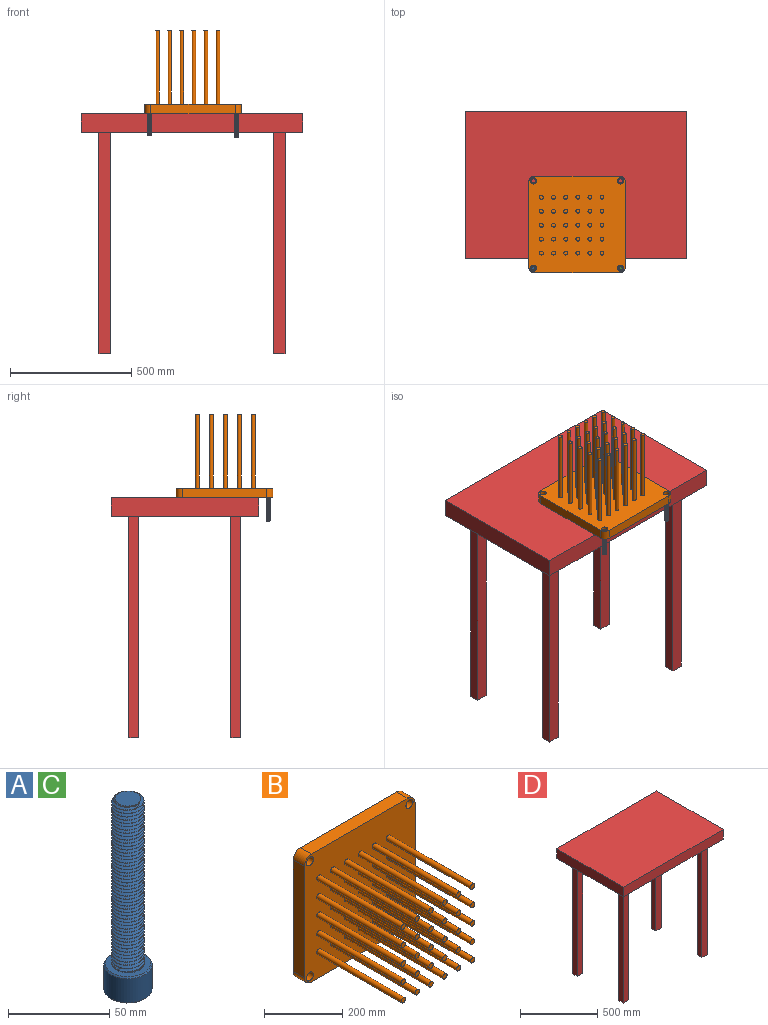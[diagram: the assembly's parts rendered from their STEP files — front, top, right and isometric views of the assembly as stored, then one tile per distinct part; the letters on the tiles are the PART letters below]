
ASSEMBLY  parts=4 mates=3
PART A: 74 faces, bbox 27.1x27.1x119.6 mm
  f0: cone r=8mm half-angle=67.5deg, axis (0,0,-1), area 33.3mm2, adj f6,f56,f57,f58
  f1: cone r=12mm half-angle=45deg, axis (0,0,-1), area 74.5mm2, adj f4,f61
  f2: cone r=11.28mm half-angle=45deg, axis (0,0,1), area 74.5mm2, adj f4,f60
  f3: cone r=8.08mm half-angle=45deg, axis (0,0,-1), area 6.2mm2, adj f60,f72
  f4: cylinder r=12mm len=24mm, axis (0,0,1), area 1097.8mm2, adj f1,f2
  f5: cone r=6.45mm half-angle=55deg, axis (0,0,-1), area 48.6mm2, adj f6,f7,f57,f58,f59
  f6: cylinder r=6.7mm len=98.78mm, axis (0,0,-1), area 519.9mm2, adj f0,f5,f57,f58
  f7: cylinder r=8mm len=16mm, axis (0,0,1), area 9.7mm2, adj f5,f8,f57,f58
  f8: cylinder r=8mm len=16mm, axis (0,0,1), area 12.6mm2, adj f7,f9,f57,f58
  f9: cylinder r=8mm len=16mm, axis (0,0,1), area 12.6mm2, adj f8,f10,f57,f58
  f10: cylinder r=8mm len=16mm, axis (0,0,1), area 12.6mm2, adj f9,f11,f57,f58
  f11: cylinder r=8mm len=16mm, axis (0,0,1), area 12.6mm2, adj f10,f12,f57,f58
  f12: cylinder r=8mm len=16mm, axis (0,0,1), area 12.6mm2, adj f11,f13,f57,f58
  f13: cylinder r=8mm len=16mm, axis (0,0,1), area 12.6mm2, adj f12,f14,f57,f58
  f14: cylinder r=8mm len=16mm, axis (0,0,1), area 12.6mm2, adj f13,f15,f57,f58
  f15: cylinder r=8mm len=16mm, axis (0,0,1), area 12.6mm2, adj f14,f16,f57,f58
  f16: cylinder r=8mm len=16mm, axis (0,0,1), area 12.6mm2, adj f15,f17,f57,f58
  f17: cylinder r=8mm len=16mm, axis (0,0,1), area 12.6mm2, adj f16,f18,f57,f58
  f18: cylinder r=8mm len=16mm, axis (0,0,1), area 12.6mm2, adj f17,f19,f57,f58
  f19: cylinder r=8mm len=16mm, axis (0,0,1), area 12.6mm2, adj f18,f20,f57,f58
  f20: cylinder r=8mm len=16mm, axis (0,0,1), area 12.6mm2, adj f19,f21,f57,f58
  f21: cylinder r=8mm len=16mm, axis (0,0,1), area 12.6mm2, adj f20,f22,f57,f58
  f22: cylinder r=8mm len=16mm, axis (0,0,1), area 12.6mm2, adj f21,f23,f57,f58
  f23: cylinder r=8mm len=16mm, axis (0,0,1), area 12.6mm2, adj f22,f24,f57,f58
  f24: cylinder r=8mm len=16mm, axis (0,0,1), area 12.6mm2, adj f23,f25,f57,f58
  f25: cylinder r=8mm len=16mm, axis (0,0,1), area 12.6mm2, adj f24,f26,f57,f58
  f26: cylinder r=8mm len=16mm, axis (0,0,1), area 12.6mm2, adj f25,f27,f57,f58
  f27: cylinder r=8mm len=16mm, axis (0,0,1), area 12.6mm2, adj f26,f28,f57,f58
  f28: cylinder r=8mm len=16mm, axis (0,0,1), area 12.6mm2, adj f27,f29,f57,f58
  f29: cylinder r=8mm len=16mm, axis (0,0,1), area 12.6mm2, adj f28,f30,f57,f58
  f30: cylinder r=8mm len=16mm, axis (0,0,1), area 12.6mm2, adj f29,f31,f57,f58
  f31: cylinder r=8mm len=16mm, axis (0,0,1), area 12.6mm2, adj f30,f32,f57,f58
  f32: cylinder r=8mm len=16mm, axis (0,0,1), area 12.6mm2, adj f31,f33,f57,f58
  f33: cylinder r=8mm len=16mm, axis (0,0,1), area 12.6mm2, adj f32,f34,f57,f58
  f34: cylinder r=8mm len=16mm, axis (0,0,1), area 12.6mm2, adj f33,f35,f57,f58
  f35: cylinder r=8mm len=16mm, axis (0,0,1), area 12.6mm2, adj f34,f36,f57,f58
  f36: cylinder r=8mm len=16mm, axis (0,0,1), area 12.6mm2, adj f35,f37,f57,f58
  f37: cylinder r=8mm len=16mm, axis (0,0,1), area 12.6mm2, adj f36,f38,f57,f58
  f38: cylinder r=8mm len=16mm, axis (0,0,1), area 12.6mm2, adj f37,f39,f57,f58
  f39: cylinder r=8mm len=16mm, axis (0,0,1), area 12.6mm2, adj f38,f40,f57,f58
  f40: cylinder r=8mm len=16mm, axis (0,0,1), area 12.6mm2, adj f39,f41,f57,f58
  f41: cylinder r=8mm len=16mm, axis (0,0,1), area 12.6mm2, adj f40,f42,f57,f58
  f42: cylinder r=8mm len=16mm, axis (0,0,1), area 12.6mm2, adj f41,f43,f57,f58
  f43: cylinder r=8mm len=16mm, axis (0,0,1), area 12.6mm2, adj f42,f44,f57,f58
  f44: cylinder r=8mm len=16mm, axis (0,0,1), area 12.6mm2, adj f43,f45,f57,f58
  f45: cylinder r=8mm len=16mm, axis (0,0,1), area 12.6mm2, adj f44,f46,f57,f58
  f46: cylinder r=8mm len=16mm, axis (0,0,1), area 12.6mm2, adj f45,f47,f57,f58
  f47: cylinder r=8mm len=16mm, axis (0,0,1), area 12.6mm2, adj f46,f48,f57,f58
  f48: cylinder r=8mm len=16mm, axis (0,0,1), area 12.6mm2, adj f47,f49,f57,f58
  f49: cylinder r=8mm len=16mm, axis (0,0,1), area 12.6mm2, adj f48,f50,f57,f58
  f50: cylinder r=8mm len=16mm, axis (0,0,1), area 12.6mm2, adj f49,f51,f57,f58
  f51: cylinder r=8mm len=16mm, axis (0,0,1), area 12.6mm2, adj f50,f52,f57,f58
  f52: cylinder r=8mm len=16mm, axis (0,0,1), area 12.6mm2, adj f51,f53,f57,f58
  f53: cylinder r=8mm len=16mm, axis (0,0,1), area 12.6mm2, adj f52,f54,f57,f58
  f54: cylinder r=8mm len=16mm, axis (0,0,1), area 12.6mm2, adj f53,f55,f57,f58
  f55: cylinder r=8mm len=16mm, axis (0,0,1), area 12.6mm2, adj f54,f56,f57,f58
  f56: cylinder r=8mm len=16mm, axis (0,0,1), area 30.7mm2, adj f0,f55,f57,f58,f61
  f57: bspline ~100.82x15.98mm, area 3416.9mm2, adj f0,f5,f6,f7,f8,f9,f10,f11
  f58: bspline ~99.53x12.99mm, area 3417.4mm2, adj f0,f5,f6,f7,f8,f9,f10,f11
  f59: plane 12.89x12.89mm, normal (0,0,1), area 130.6mm2, adj f5
  f60: plane 25.19x25.19mm, normal (0,0,-1), area 194.5mm2, adj f2,f3,f62,f63,f64,f65,f66
  f61: plane 22.56x22.56mm, normal (0,0,1), area 198.7mm2, adj f1,f56
  f62: cone r=8.08mm half-angle=45deg, axis (0,0,-1), area 0mm2, adj f60,f68
  f63: cone r=8.08mm half-angle=45deg, axis (0,0,-1), area 0mm2, adj f60,f69
  f64: cone r=8.08mm half-angle=45deg, axis (0,0,-1), area 0mm2, adj f60,f70
  f65: cone r=8.08mm half-angle=45deg, axis (0,0,-1), area 0mm2, adj f60,f71
  f66: cone r=8.08mm half-angle=45deg, axis (0,0,-1), area 0mm2, adj f60,f73
  f67: plane 16.17x14mm, normal (0,0,-1), area 169.7mm2, adj f68,f69,f70,f71,f72,f73
  f68: plane 13.56x10.06mm, normal (-0.5,-0.87,0), area 79mm2, adj f62,f67,f69,f73
  f69: plane 13.56x11.15mm, normal (-1,0,0), area 79.1mm2, adj f63,f67,f68,f70
  f70: plane 13.56x10.06mm, normal (-0.5,0.87,0), area 79mm2, adj f64,f67,f69,f71
  f71: plane 13.56x10.06mm, normal (0.5,0.87,0), area 79.1mm2, adj f65,f67,f70,f72
  f72: plane 11.29x8.87mm, normal (1,0,0), area 79.1mm2, adj f3,f67,f71,f73
  f73: plane 13.56x10.06mm, normal (0.5,-0.87,0), area 79.1mm2, adj f66,f67,f68,f72
PART B: 82 faces, bbox 400x344.8x400 mm
  f0: plane 349.2x40mm, normal (-1,0,0), area 13968mm2, adj f4,f5,f18,f21
  f1: plane 349.2x40mm, normal (0,0,-1), area 13968mm2, adj f4,f5,f18,f19
  f2: plane 349.2x40mm, normal (1,0,0), area 13968mm2, adj f4,f5,f19,f20
  f3: plane 349.2x40mm, normal (0,0,1), area 13968mm2, adj f4,f5,f20,f21
  f4: plane 400x400mm, normal (0,-1,0), area 151643.8mm2, adj f0,f1,f2,f3,f8,f11,f14,f17
  f5: plane 400x400mm, normal (0,1,0), area 158484.1mm2, adj f0,f1,f2,f3,f6,f9,f12,f15
  f6: cylinder r=8.75mm len=20mm, axis (0,-1,0), area 1099.6mm2, adj f5,f7
  f7: plane 25.5x25.5mm, normal (0,-1,0), area 270.2mm2, adj f6,f8
  f8: cylinder r=12.75mm len=25.5mm, axis (0,-1,0), area 1602.2mm2, adj f4,f7
  f9: cylinder r=8.75mm len=20mm, axis (0,-1,0), area 1099.6mm2, adj f5,f10
  f10: plane 25.5x25.5mm, normal (0,-1,0), area 270.2mm2, adj f9,f11
  f11: cylinder r=12.75mm len=25.5mm, axis (0,-1,0), area 1602.2mm2, adj f4,f10
  f12: cylinder r=8.75mm len=20mm, axis (0,-1,0), area 1099.6mm2, adj f5,f13
  f13: plane 25.5x25.5mm, normal (0,-1,0), area 270.2mm2, adj f12,f14
  f14: cylinder r=12.75mm len=25.5mm, axis (0,-1,0), area 1602.2mm2, adj f4,f13
  f15: cylinder r=8.75mm len=20mm, axis (0,-1,0), area 1099.6mm2, adj f5,f16
  f16: plane 25.5x25.5mm, normal (0,-1,0), area 270.2mm2, adj f15,f17
  f17: cylinder r=12.75mm len=25.5mm, axis (0,-1,0), area 1602.2mm2, adj f4,f16
  f18: cylinder r=25.4mm len=40mm, axis (0,-1,0), area 1595.9mm2, adj f0,f1,f4,f5
  f19: cylinder r=25.4mm len=40mm, axis (0,1,0), area 1595.9mm2, adj f1,f2,f4,f5
  f20: cylinder r=25.4mm len=40mm, axis (0,-1,0), area 1595.9mm2, adj f2,f3,f4,f5
  f21: cylinder r=25.4mm len=40mm, axis (0,1,0), area 1595.9mm2, adj f0,f3,f4,f5
  f22: cylinder r=7.82mm len=304.8mm, axis (0,1,0), area 14971.1mm2, adj f4,f23
  f23: plane 15.63x15.63mm, normal (0,-1,0), area 192mm2, adj f22
  f24: cylinder r=7.82mm len=304.8mm, axis (0,1,0), area 14971.1mm2, adj f4,f25
  f25: plane 15.63x15.63mm, normal (0,-1,0), area 192mm2, adj f24
  f26: cylinder r=7.82mm len=304.8mm, axis (0,1,0), area 14971.1mm2, adj f4,f27
  f27: plane 15.63x15.63mm, normal (0,-1,0), area 192mm2, adj f26
  f28: cylinder r=7.82mm len=304.8mm, axis (0,1,0), area 14971.1mm2, adj f4,f29
  f29: plane 15.63x15.63mm, normal (0,-1,0), area 192mm2, adj f28
  f30: cylinder r=7.82mm len=304.8mm, axis (0,1,0), area 14971.1mm2, adj f4,f31
  f31: plane 15.63x15.63mm, normal (0,-1,0), area 192mm2, adj f30
  f32: cylinder r=7.82mm len=304.8mm, axis (0,1,0), area 14971.1mm2, adj f4,f33
  f33: plane 15.63x15.63mm, normal (0,-1,0), area 192mm2, adj f32
  f34: cylinder r=7.82mm len=304.8mm, axis (0,1,0), area 14971.1mm2, adj f4,f35
  f35: plane 15.63x15.63mm, normal (0,-1,0), area 192mm2, adj f34
  f36: cylinder r=7.82mm len=304.8mm, axis (0,1,0), area 14971.1mm2, adj f4,f37
  f37: plane 15.63x15.63mm, normal (0,-1,0), area 192mm2, adj f36
  f38: cylinder r=7.82mm len=304.8mm, axis (0,1,0), area 14971.1mm2, adj f4,f39
  f39: plane 15.63x15.63mm, normal (0,-1,0), area 192mm2, adj f38
  f40: cylinder r=7.82mm len=304.8mm, axis (0,1,0), area 14971.1mm2, adj f4,f41
  f41: plane 15.63x15.63mm, normal (0,-1,0), area 192mm2, adj f40
  f42: cylinder r=7.82mm len=304.8mm, axis (0,1,0), area 14971.1mm2, adj f4,f43
  f43: plane 15.63x15.63mm, normal (0,-1,0), area 192mm2, adj f42
  f44: cylinder r=7.82mm len=304.8mm, axis (0,1,0), area 14971.1mm2, adj f4,f45
  f45: plane 15.63x15.63mm, normal (0,-1,0), area 192mm2, adj f44
  f46: cylinder r=7.82mm len=304.8mm, axis (0,1,0), area 14971.1mm2, adj f4,f47
  f47: plane 15.63x15.63mm, normal (0,-1,0), area 192mm2, adj f46
  f48: cylinder r=7.82mm len=304.8mm, axis (0,1,0), area 14971.1mm2, adj f4,f49
  f49: plane 15.63x15.63mm, normal (0,-1,0), area 192mm2, adj f48
  f50: cylinder r=7.82mm len=304.8mm, axis (0,1,0), area 14971.1mm2, adj f4,f51
  f51: plane 15.63x15.63mm, normal (0,-1,0), area 192mm2, adj f50
  f52: cylinder r=7.82mm len=304.8mm, axis (0,1,0), area 14971.1mm2, adj f4,f53
  f53: plane 15.63x15.63mm, normal (0,-1,0), area 192mm2, adj f52
  f54: cylinder r=7.82mm len=304.8mm, axis (0,1,0), area 14971.1mm2, adj f4,f55
  f55: plane 15.63x15.63mm, normal (0,-1,0), area 192mm2, adj f54
  f56: cylinder r=7.82mm len=304.8mm, axis (0,1,0), area 14971.1mm2, adj f4,f57
  f57: plane 15.63x15.63mm, normal (0,-1,0), area 192mm2, adj f56
  f58: cylinder r=7.82mm len=304.8mm, axis (0,1,0), area 14971.1mm2, adj f4,f59
  f59: plane 15.63x15.63mm, normal (0,-1,0), area 192mm2, adj f58
  f60: cylinder r=7.82mm len=304.8mm, axis (0,1,0), area 14971.1mm2, adj f4,f61
  f61: plane 15.63x15.63mm, normal (0,-1,0), area 192mm2, adj f60
  f62: cylinder r=7.82mm len=304.8mm, axis (0,1,0), area 14971.1mm2, adj f4,f63
  f63: plane 15.63x15.63mm, normal (0,-1,0), area 192mm2, adj f62
  f64: cylinder r=7.82mm len=304.8mm, axis (0,1,0), area 14971.1mm2, adj f4,f65
  f65: plane 15.63x15.63mm, normal (0,-1,0), area 192mm2, adj f64
  f66: cylinder r=7.82mm len=304.8mm, axis (0,1,0), area 14971.1mm2, adj f4,f67
  f67: plane 15.63x15.63mm, normal (0,-1,0), area 192mm2, adj f66
  f68: cylinder r=7.82mm len=304.8mm, axis (0,1,0), area 14971.1mm2, adj f4,f69
  f69: plane 15.63x15.63mm, normal (0,-1,0), area 192mm2, adj f68
  f70: cylinder r=7.82mm len=304.8mm, axis (0,1,0), area 14971.1mm2, adj f4,f71
  f71: plane 15.63x15.63mm, normal (0,-1,0), area 192mm2, adj f70
  f72: cylinder r=7.82mm len=304.8mm, axis (0,1,0), area 14971.1mm2, adj f4,f73
  f73: plane 15.63x15.63mm, normal (0,-1,0), area 192mm2, adj f72
  f74: cylinder r=7.82mm len=304.8mm, axis (0,1,0), area 14971.1mm2, adj f4,f75
  f75: plane 15.63x15.63mm, normal (0,-1,0), area 192mm2, adj f74
  f76: cylinder r=7.82mm len=304.8mm, axis (0,1,0), area 14971.1mm2, adj f4,f77
  f77: plane 15.63x15.63mm, normal (0,-1,0), area 192mm2, adj f76
  f78: cylinder r=7.82mm len=304.8mm, axis (0,1,0), area 14971.1mm2, adj f4,f79
  f79: plane 15.63x15.63mm, normal (0,-1,0), area 192mm2, adj f78
  f80: cylinder r=7.82mm len=304.8mm, axis (0,1,0), area 14971.1mm2, adj f4,f81
  f81: plane 15.63x15.63mm, normal (0,-1,0), area 192mm2, adj f80
PART C: same geometry as A
PART D: 26 faces, bbox 914.4x609.6x990.6 mm
  f0: plane 914.4x609.6mm, normal (0,0,-1), area 549338.7mm2, adj f1,f2,f3,f4,f6,f7,f8,f9
  f1: plane 609.6x76.2mm, normal (-1,0,0), area 46451.5mm2, adj f0,f2,f4,f5
  f2: plane 914.4x76.2mm, normal (0,-1,0), area 69677.3mm2, adj f0,f1,f3,f5
  f3: plane 609.6x76.2mm, normal (1,0,0), area 46451.5mm2, adj f0,f2,f4,f5
  f4: plane 914.4x76.2mm, normal (0,1,0), area 69677.3mm2, adj f0,f1,f3,f5
  f5: plane 914.4x609.6mm, normal (0,0,1), area 557418.2mm2, adj f1,f2,f3,f4
  f6: plane 914.4x41.12mm, normal (-1,0,0), area 37602.4mm2, adj f0,f7,f9,f10
  f7: plane 914.4x49.12mm, normal (0,1,0), area 44914mm2, adj f0,f6,f8,f10
  f8: plane 914.4x41.12mm, normal (1,0,0), area 37602.4mm2, adj f0,f7,f9,f10
  f9: plane 914.4x49.12mm, normal (0,-1,0), area 44914mm2, adj f0,f6,f8,f10
  f10: plane 49.12x41.12mm, normal (0,0,-1), area 2019.9mm2, adj f6,f7,f8,f9
  f11: plane 914.4x49.12mm, normal (0,-1,0), area 44914mm2, adj f0,f12,f14,f15
  f12: plane 914.4x41.12mm, normal (-1,0,0), area 37602.4mm2, adj f0,f11,f13,f15
  f13: plane 914.4x49.12mm, normal (0,1,0), area 44914mm2, adj f0,f12,f14,f15
  f14: plane 914.4x41.12mm, normal (1,0,0), area 37602.4mm2, adj f0,f11,f13,f15
  f15: plane 49.12x41.12mm, normal (0,0,-1), area 2019.9mm2, adj f11,f12,f13,f14
  f16: plane 914.4x49.12mm, normal (0,1,0), area 44914mm2, adj f0,f17,f19,f20
  f17: plane 914.4x41.12mm, normal (1,0,0), area 37602.4mm2, adj f0,f16,f18,f20
  f18: plane 914.4x49.12mm, normal (0,-1,0), area 44914mm2, adj f0,f17,f19,f20
  f19: plane 914.4x41.12mm, normal (-1,0,0), area 37602.4mm2, adj f0,f16,f18,f20
  f20: plane 49.12x41.12mm, normal (0,0,-1), area 2019.9mm2, adj f16,f17,f18,f19
  f21: plane 914.4x49.12mm, normal (0,1,0), area 44914mm2, adj f0,f22,f24,f25
  f22: plane 914.4x41.12mm, normal (1,0,0), area 37602.4mm2, adj f0,f21,f23,f25
  f23: plane 914.4x49.12mm, normal (0,-1,0), area 44914mm2, adj f0,f22,f24,f25
  f24: plane 914.4x41.12mm, normal (-1,0,0), area 37602.4mm2, adj f0,f21,f23,f25
  f25: plane 49.12x41.12mm, normal (0,0,-1), area 2019.9mm2, adj f21,f22,f23,f24
PLACE A rot(axis=(0.71,-0.71,0),180deg) t=(-94.31,-393.44,106.56)mm
PLACE B rot(axis=(-1,0,0),90deg) t=(-114.31,-413.44,194.56)mm
PLACE C rot(axis=(0.71,-0.71,0),180deg) t=(265.69,-393.44,96.56)mm
PLACE D t=(-375.77,-354.32,118.36)mm
MATE cylindrical C.f1 <-> B.f12  axis (0,0,-1) through (265.69,-393.44,204.56)mm
MATE planar B.f5 <-> D.f5  axis (0,0,-1) through (85.69,-213.44,194.56)mm
MATE cylindrical A.f1 <-> B.f15  axis (0,0,-1) through (-94.31,-393.44,214.56)mm
